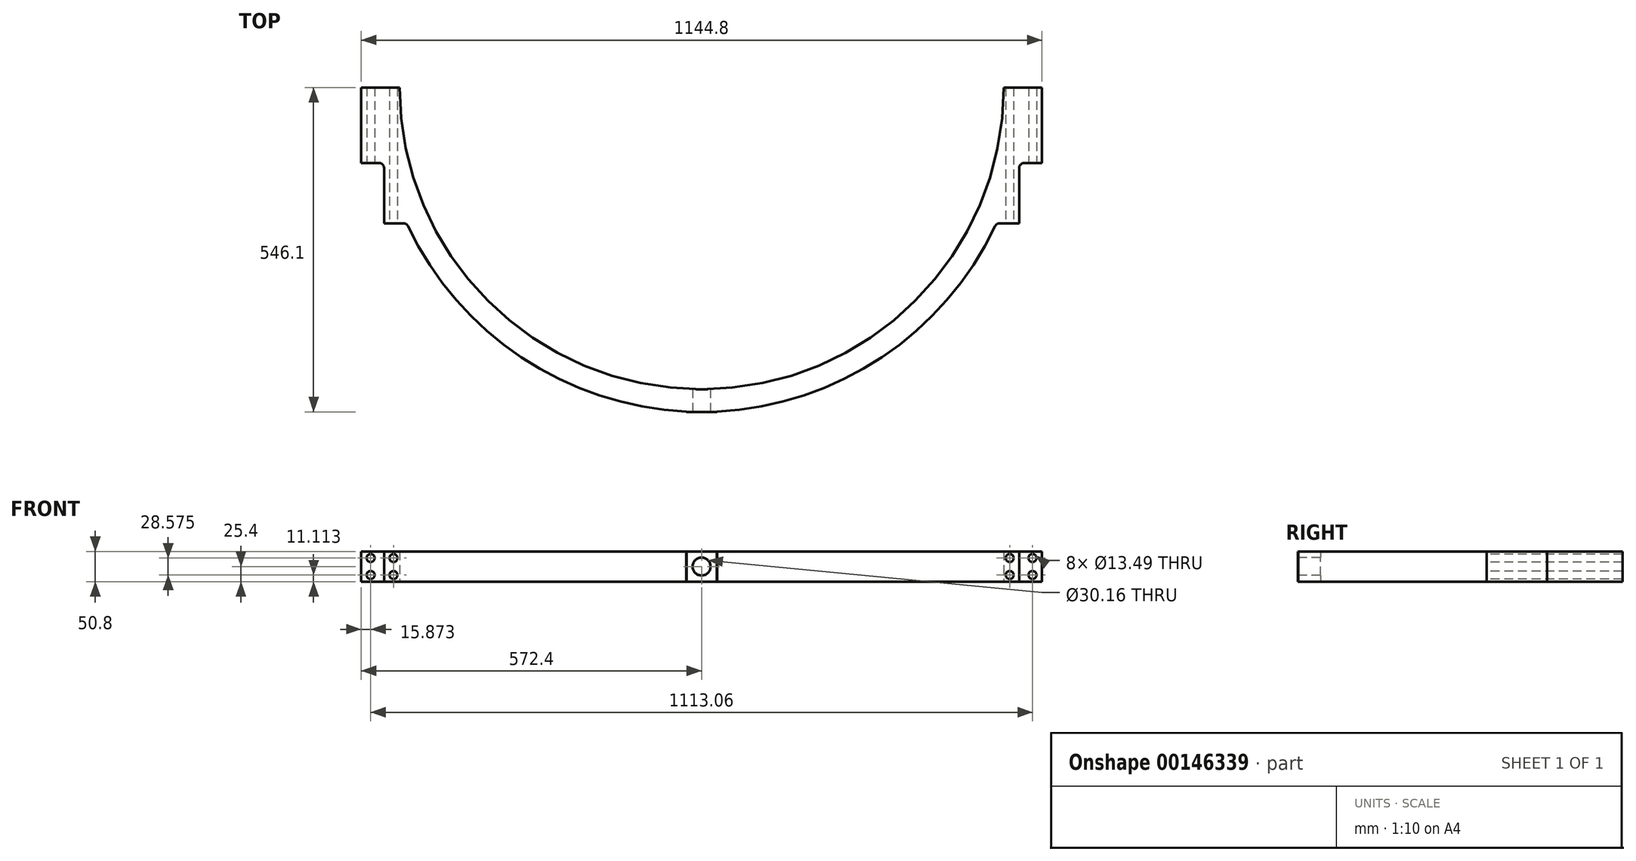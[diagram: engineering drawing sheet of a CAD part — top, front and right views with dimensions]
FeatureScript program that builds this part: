
annotation { "Feature Type Name" : "Feature", "Feature Type Description" : "" }
export const myFeature = defineFeature(function(context is Context, id is Id, definition is map)
    precondition{}
    {
        {
            var Q0;
            Q0=qCreatedBy(makeId("Top.planeOp"),FACE);
            var sketch = newSketch(context, id + "F0", { "sketchPlane" : qUnion([Q0])});
            skArc(sketch, "E0", {"start": v(-508, 0) * mm, "mid": v(-359.21, -359.21) * mm, "end": v(0, -508) * mm});
            skArc(sketch, "E1", {"start": v(-546.1, 0) * mm, "mid": v(-542.34, -63.94) * mm, "end": v(-531.13, -127) * mm, "construction": true});
            skLineSegment(sketch, "E2", {"start": v(-508, 0) * mm, "end": v(-546.1, 0) * mm});
            skLineSegment(sketch, "E3", {"start": v(-546.1, 0) * mm, "end": v(-572.4, 0) * mm});
            skLineSegment(sketch, "E4", {"start": v(-572.4, 0) * mm, "end": v(-572.4, -127) * mm});
            skLineSegment(sketch, "E5", {"start": v(-572.4, -127) * mm, "end": v(-542.52, -127) * mm});
            skLineSegment(sketch, "E6", {"start": v(0, -546.1) * mm, "end": v(0, -508) * mm});
            skLineSegment(sketch, "E7", {"start": v(0, -508) * mm, "end": v(0, 0) * mm, "construction": true});
            skArc(sketch, "E8", {"start": v(-531.13, -127) * mm, "mid": v(-516.05, -178.67) * mm, "end": v(-495.95, -228.6) * mm, "construction": true});
            skPoint(sketch, "E9.visualSharp", {"position": v(-531.13, -127) * mm});
            skLineSegment(sketch, "E10", {"start": v(-501.34, -228.6) * mm, "end": v(-534.05, -228.6) * mm});
            skLineSegment(sketch, "E11", {"start": v(-534.05, -228.6) * mm, "end": v(-534.05, -135.47) * mm});
            skLineSegment(sketch, "E12", {"start": v(-508, -228.6) * mm, "end": v(-508, 0) * mm, "construction": true});
            skArc(sketch, "E13", {"start": v(-493.69, -233.45) * mm, "mid": v(-303.1, -454.27) * mm, "end": v(-26.02, -545.48) * mm});
            skPoint(sketch, "E14.visualSharp", {"position": v(-495.95, -228.6) * mm});
            skArc(sketch, "E14.filletArc", {"start": v(-493.69, -233.45) * mm, "mid": v(-496.81, -229.91) * mm, "end": v(-501.34, -228.6) * mm});
            skPoint(sketch, "E15.newPointB", {"position": v(-534.05, -127) * mm});
            skArc(sketch, "E15.filletArc", {"start": v(-534.05, -135.47) * mm, "mid": v(-536.53, -129.48) * mm, "end": v(-542.52, -127) * mm});
            skLineSegment(sketch, "E16", {"start": v(0, -546.1) * mm, "end": v(-25.4, -546.1) * mm});
            skLineSegment(sketch, "E17", {"start": v(-25.4, -546.1) * mm, "end": v(-26.02, -545.48) * mm});
            skArc(sketch, "E18", {"start": v(-26.02, -545.48) * mm, "mid": v(-13.01, -545.94) * mm, "end": v(0, -546.1) * mm, "construction": true});
            skSolve(sketch);
        }
        {
            var Q0;
            Q0 = qSketchRegion(id + "F0", true);
            extrude(context, id + "F1", {"entities" : qUnion([Q0]), "depth" : 50.8 * mm});
        }
        {
            var Q0;
            Q0=makeQuery(id+"F1.opExtrude","SWEPT_FACE",FACE,{"disambiguationData":[OSD([sQuery(id+"F0.wireOp",EDGE,"E5")])]});
            var sketch = newSketch(context, id + "F2", { "sketchPlane" : qUnion([Q0])});
            skLineSegment(sketch, "E19", {"start": v(-572.4, 25.4) * mm, "end": v(-572.4, 25.4) * mm});
            skPoint(sketch, "E20", {"position": v(-556.53, 25.4) * mm});
            skLineSegment(sketch, "E21", {"start": v(-556.53, 11.11) * mm, "end": v(-556.53, 39.69) * mm, "construction": true});
            skSolve(sketch);
        }
        {
            var Q0;
            Q0=makeQuery(id+"F1.opExtrude","SWEPT_FACE",FACE,{"disambiguationData":[OSD([sQuery(id+"F0.wireOp",EDGE,"E10")])]});
            var sketch = newSketch(context, id + "F3", { "sketchPlane" : qUnion([Q0])});
            skLineSegment(sketch, "E22", {"start": v(-534.05, 25.4) * mm, "end": v(-518.18, 25.4) * mm, "construction": true});
            skLineSegment(sketch, "E23", {"start": v(-518.18, 39.69) * mm, "end": v(-518.18, 11.11) * mm, "construction": true});
            skSolve(sketch);
        }
        {
            var Q0;
            Q0=sQuery(id+"F2.wireOp",VERTEX,"E21.start");
            var Q1;
            Q1=sQuery(id+"F2.wireOp",VERTEX,"E21.end");
            var Q2;
            Q2=makeQuery(id+"F1.opExtrude","SWEPT_BODY",BODY,{"disambiguationData":[OSD([sQuery(id+"F0.wireOp",EDGE,"E0"),sQuery(id+"F0.wireOp",EDGE,"E2"),sQuery(id+"F0.wireOp",EDGE,"E3"),sQuery(id+"F0.wireOp",EDGE,"E4"),sQuery(id+"F0.wireOp",EDGE,"E5"),sQuery(id+"F0.wireOp",EDGE,"E6"),sQuery(id+"F0.wireOp",EDGE,"E8"),sQuery(id+"F0.wireOp",EDGE,"E9.filletArc")])]});
            hole(context, id + "F4", {"style" : HoleStyle.SIMPLE, "endStyle" : HoleEndStyle.THROUGH, "standardTappedOrClearance" : lookupTablePath({ "standard" : "ANSI", "fit" : "Normal (ASME)", "size" : "1/2", "type" : "Clearance" }), "standardBlindInLast" : lookupTablePath({ "fit" : "Free", "standard" : "ANSI", "size" : "1/2", "type" : "Clearance" }), "holeDiameter" : 13.5 * mm, "locations" : qUnion([Q0, Q1]), "scope" : qUnion([Q2]), "isTappedThrough" : true});
        }
        {
            var Q0;
            Q0=sQuery(id+"F3.wireOp",VERTEX,"E23.start");
            var Q1;
            Q1=sQuery(id+"F3.wireOp",VERTEX,"E23.end");
            var Q2;
            Q2=makeQuery(id+"F1.opExtrude","SWEPT_BODY",BODY,{"disambiguationData":[OSD([sQuery(id+"F0.wireOp",EDGE,"E0"),sQuery(id+"F0.wireOp",EDGE,"E2"),sQuery(id+"F0.wireOp",EDGE,"E3"),sQuery(id+"F0.wireOp",EDGE,"E4"),sQuery(id+"F0.wireOp",EDGE,"E5"),sQuery(id+"F0.wireOp",EDGE,"E6"),sQuery(id+"F0.wireOp",EDGE,"E10"),sQuery(id+"F0.wireOp",EDGE,"E11"),sQuery(id+"F0.wireOp",EDGE,"E13"),sQuery(id+"F0.wireOp",EDGE,"E14.filletArc"),sQuery(id+"F0.wireOp",EDGE,"E15.filletArc")])]});
            hole(context, id + "F5", {"style" : HoleStyle.SIMPLE, "endStyle" : HoleEndStyle.THROUGH, "standardTappedOrClearance" : lookupTablePath({ "standard" : "ANSI", "fit" : "Normal (ASME)", "size" : "1/2", "type" : "Clearance" }), "standardBlindInLast" : lookupTablePath({ "fit" : "Free", "standard" : "ANSI", "size" : "1/2", "type" : "Clearance" }), "holeDiameter" : 13.5 * mm, "locations" : qUnion([Q0, Q1]), "scope" : qUnion([Q2]), "isTappedThrough" : true});
        }
        {
            var Q0;
            Q0=makeQuery(id+"F1.opExtrude","SWEPT_BODY",BODY,{"disambiguationData":[OSD([sQuery(id+"F0.wireOp",EDGE,"E0"),sQuery(id+"F0.wireOp",EDGE,"E2"),sQuery(id+"F0.wireOp",EDGE,"E3"),sQuery(id+"F0.wireOp",EDGE,"E4"),sQuery(id+"F0.wireOp",EDGE,"E5"),sQuery(id+"F0.wireOp",EDGE,"E6"),sQuery(id+"F0.wireOp",EDGE,"E10"),sQuery(id+"F0.wireOp",EDGE,"E11"),sQuery(id+"F0.wireOp",EDGE,"E13"),sQuery(id+"F0.wireOp",EDGE,"E14.filletArc"),sQuery(id+"F0.wireOp",EDGE,"E15.filletArc"),sQuery(id+"F0.wireOp",EDGE,"E16"),sQuery(id+"F0.wireOp",EDGE,"E17")])]});
            var Q1;
            Q1=qCreatedBy(makeId("Right.planeOp"),FACE);
            mirror(context, id + "F6", {"operationType" : NewBodyOperationType.ADD, "entities" : qUnion([Q0]), "mirrorPlane" : qUnion([Q1])});
        }
        {
            var Q0;
            {var subQ0=makeQuery(id+"F1.opExtrude","SWEPT_FACE",FACE,{"disambiguationData":[OSD([sQuery(id+"F0.wireOp",EDGE,"E16")])]});Q0=makeQuery(id+"F6.boolean.opBoolean","MERGE",FACE,{"derivedFrom":[subQ0,makeQuery(id+"F6.opPattern","COPY",FACE,{"derivedFrom":subQ0,"instanceName":"1"})]});}
            var sketch = newSketch(context, id + "F7", { "sketchPlane" : qUnion([Q0])});
            skLineSegment(sketch, "E24", {"start": v(-25.4, 25.4) * mm, "end": v(25.4, 25.4) * mm, "construction": true});
            skPoint(sketch, "E25", {"position": v(0, 25.4) * mm});
            skSolve(sketch);
        }
        {
            var Q0;
            Q0=sQuery(id+"F7.wireOp",VERTEX,"E25");
            var Q1;
            Q1=makeQuery(id+"F1.opExtrude","SWEPT_BODY",BODY,{"disambiguationData":[OSD([sQuery(id+"F0.wireOp",EDGE,"E0"),sQuery(id+"F0.wireOp",EDGE,"E2"),sQuery(id+"F0.wireOp",EDGE,"E3"),sQuery(id+"F0.wireOp",EDGE,"E4"),sQuery(id+"F0.wireOp",EDGE,"E5"),sQuery(id+"F0.wireOp",EDGE,"E6"),sQuery(id+"F0.wireOp",EDGE,"E10"),sQuery(id+"F0.wireOp",EDGE,"E11"),sQuery(id+"F0.wireOp",EDGE,"E13"),sQuery(id+"F0.wireOp",EDGE,"E14.filletArc"),sQuery(id+"F0.wireOp",EDGE,"E15.filletArc"),sQuery(id+"F0.wireOp",EDGE,"E16"),sQuery(id+"F0.wireOp",EDGE,"E17")])]});
            hole(context, id + "F8", {"style" : HoleStyle.SIMPLE, "endStyle" : HoleEndStyle.THROUGH, "standardTappedOrClearance" : lookupTablePath({ "standard" : "ANSI", "engagement" : "75%", "pitch" : "18 tpi", "size" : "1 1/4", "type" : "Tapped" }), "standardBlindInLast" : lookupTablePath({ "standard" : "ANSI", "engagement" : "75%", "pitch" : "18 tpi", "size" : "1 1/4", "type" : "Tapped" }), "holeDiameter" : 30.16 * mm, "locations" : qUnion([Q0]), "scope" : qUnion([Q1]), "isTappedThrough" : true, "majorDiameter" : 31.75 * mm, "showTappedDepth" : true});
        }
    });
